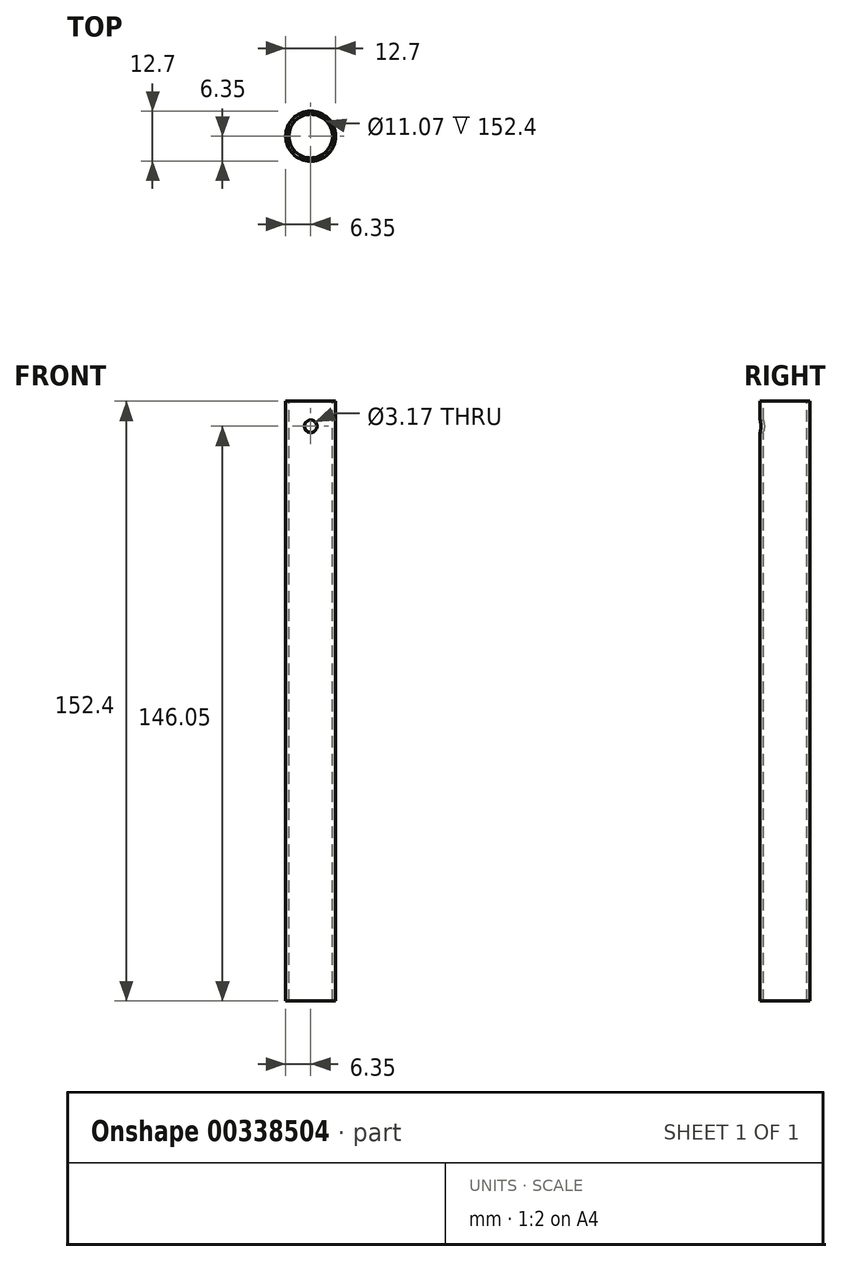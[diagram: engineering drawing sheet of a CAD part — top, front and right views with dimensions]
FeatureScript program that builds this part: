
annotation { "Feature Type Name" : "Feature", "Feature Type Description" : "" }
export const myFeature = defineFeature(function(context is Context, id is Id, definition is map)
    precondition{}
    {
        {
            var Q0;
            Q0=qCreatedBy(makeId("Top.planeOp"),FACE);
            var sketch = newSketch(context, id + "F0", { "sketchPlane" : qUnion([Q0])});
            skCircle(sketch, "E0", {"center": v(0, 0) * mm, "radius": 6.35 * mm});
            skCircle(sketch, "E1", {"center": v(0, 0) * mm, "radius": 5.54 * mm});
            skSolve(sketch);
        }
        {
            var Q0;
            Q0=makeQuery(id+"F0.imprint","IMPRINT",FACE,{"disambiguationData":[TD([[makeQuery(id+"F0.imprint","IMPRINT",EDGE,{"derivedFrom":sQuery(id+"F0.wireOp",EDGE,"E0")}),1.0]])]});
            extrude(context, id + "F1", {"entities" : qUnion([Q0]), "oppositeDirection" : true, "depth" : 152.4 * mm});
        }
        {
            var Q0;
            Q0=qCreatedBy(makeId("Front.planeOp"),FACE);
            var sketch = newSketch(context, id + "F2", { "sketchPlane" : qUnion([Q0])});
            skLineSegment(sketch, "E2", {"start": v(0, 0) * mm, "end": v(0, -6.35) * mm});
            skCircle(sketch, "E3", {"center": v(0, -6.35) * mm, "radius": 1.59 * mm});
            skSolve(sketch);
        }
        {
            var Q0;
            Q0=makeQuery(id+"F2.imprint","IMPRINT",FACE,{"disambiguationData":[TD([[makeQuery(id+"F2.imprint","IMPRINT",EDGE,{"derivedFrom":sQuery(id+"F2.wireOp",EDGE,"E3")}),1.0]])]});
            extrude(context, id + "F3", {"entities" : qUnion([Q0]), "operationType" : NewBodyOperationType.REMOVE, "depth" : 25.4 * mm});
        }
    });
